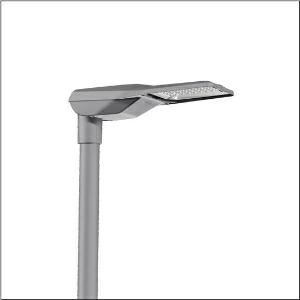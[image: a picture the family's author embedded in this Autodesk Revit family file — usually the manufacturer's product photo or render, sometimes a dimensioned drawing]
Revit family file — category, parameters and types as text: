
# Revit family: streetlight_sl_21_iq_mini___st0_5a_5xe2b31d08jb_7d26
name_source: partatom
category: Lighting Fixtures
units: mm (PartAtom-declared; Revit-internal decimal feet)

## family parameters
Cut with Voids When Loaded = No
Host = Face
Light Source = No
Part Type = Normal
Room Calculation Point = No
Round Connector Dimension = Use Diameter
Shared = No

## types (1)
- --- (1 x LED, 10820 lm, 71.6 W, 3000K)
    Apparent Load = 72 VA
    CIE Flux Codes = 43 76 97 100 100
    Color Rendering = 70
    Color Temperature = 3000K
    Default Elevation = 1800 mm
    Description = Streetlight SL 21 iQ mini, mast luminaire, primary light control with lens, of PMMA, primary optical cover: cover, of toughened safety glass, transparent, light distribution: ST0.5a, light emission: direct distribution, primary light characteristic: asymmetric, installation type: post-top, side-entry, LED, High Power LED, rated luminous flux: 10.820lm, luminous efficacy: 151lm/W, light colour: 730, colour temperature: 3000K, control: Auto-Match, Temp-Guard, Lumen-Switch, Night-Set, Smart-Wire, Light-Fading, Desk-Remote (wireless, voltage-free reading and setting of iQ features in the workshop via application-optimized NFC function/RFID function), optimised constant luminous flux control (CLO 2.0), presetting dimming linear, mains connection: 220..240V, AC, 50/60Hz, start of lifetime: 72W, end of service life: 75W, reduction: 33W, luminaire housing, of diecast aluminium, powder-coated, Siteco® metallic grey (DB 702S), corrosivity category C5 mid according to DIN EN ISO 12944, please order mast flange separately, inclination adjustable: 0°, 5°, 10°, 15°, sealing non-destructively replaceable, multi-level sealing system, length: 628mm, width: 235mm, height: 110mm, mast flange for spigot size: 42mm (side-entry): 5XC10008XM4, 60/48mm (side-entry/post-top): 5XC10108XM2, 76/60mm (side-entry/post-top): 5XC10108XM1, protection rating (complete): IP66, insulation class (complete): insulation class II (safety insulation), certification: CE, ENEC, ENEC+, VDE, impact resistance: IK09, permissible operating ambient temperature for outdoor applications: -40..+50°C, standard-compliant lighting for roads and squares, packaging unit: 1 piece

Light Distribution: ST0.5a
    Height = 110 mm
    Lamp = 1 x LED
    Lamp Light Flux = 10820 lm
    Lamp Power = 71.6 W
    Lamp count = 1
    Length = 625 mm
    Luminous efficacy = 151 lm/W
    Manufacturer = Siteco
    ModVariant = No
    Model = 5XE2B31D08JB
    Number of Poles = 1
    OnlyDefault = Yes
    Power Factor = 1
    Product Name = Streetlight SL 21 iQ mini | ST0.5a
    Product group = mast luminaire | pylon top
    ProductGroupID = 6100
    Protection Class = Protection class II
    Protection Degree = IP 66
    RLX_Detail_Level = 1
    RLX_Emergency_Light_Flux = 0 lm
    RLX_Emergency_Type = 0
    RLX_Emergency_Type_DB = No
    RlxData = <blob elided: 103693 chars, md5=2d981065>
    Socket = socket
    Standby Power = 0 W
    System Light Flux = 10820 lm
    System Power = 72 W
    Type Comments = factory setting: luminous flux: 100 % | dim-lin: 254 | 746 mA
    Type Image = l_1003519.jpg
    URL = http://relux.com
    VarID = @adj_122743
    Voltage = 0 V
    Weight = 0.00 kg
    Width = 234 mm

## geometry (parser evidence)
native form markers: Blend x4, Sweep x10
no freeform markers — native parametric forms only
